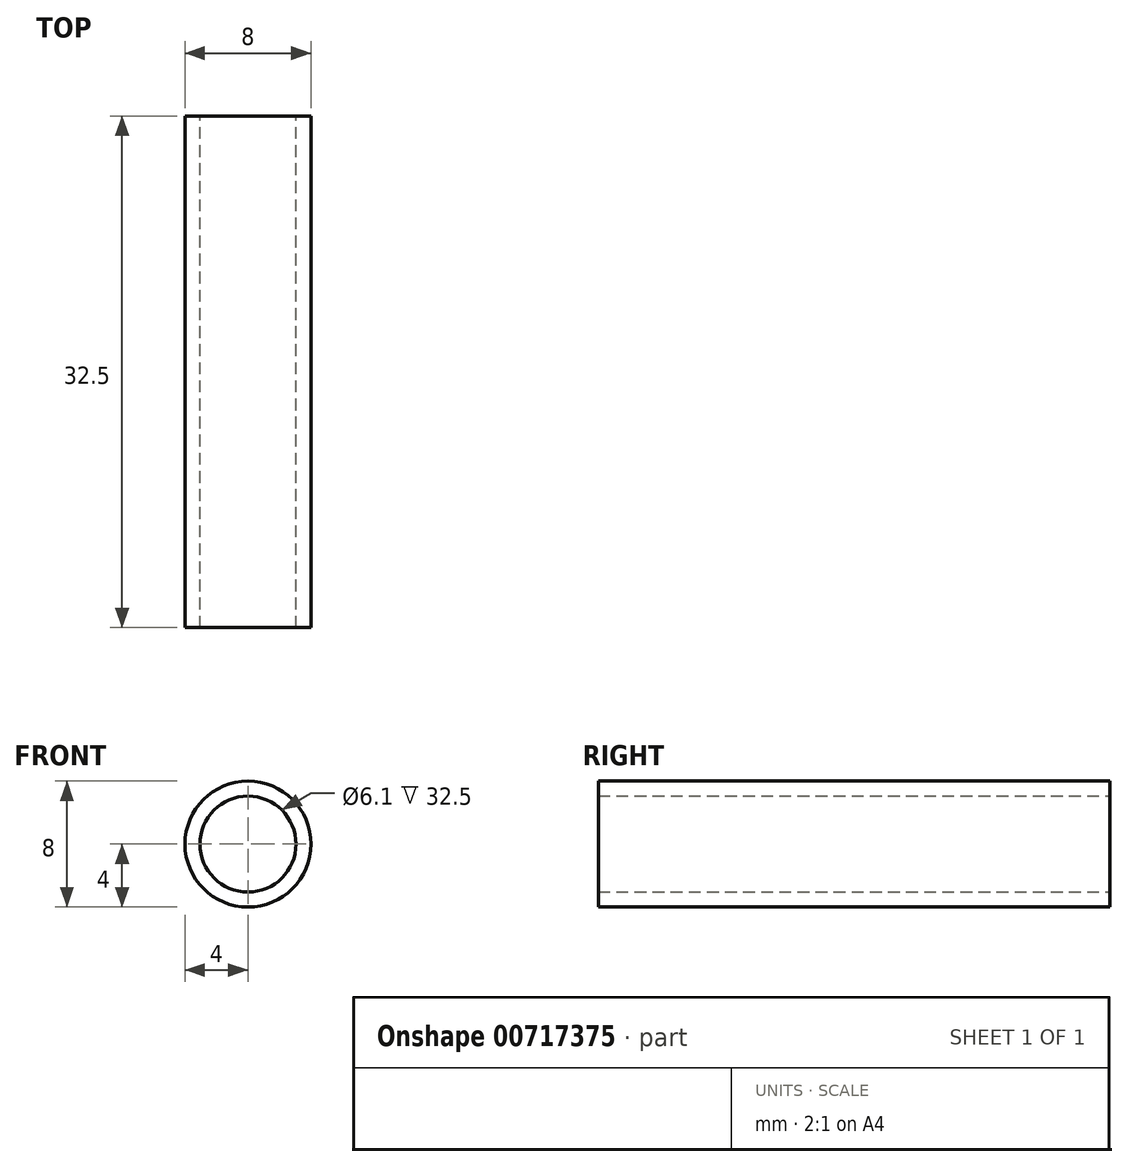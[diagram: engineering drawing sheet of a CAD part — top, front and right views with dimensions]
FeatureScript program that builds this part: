
annotation { "Feature Type Name" : "Feature", "Feature Type Description" : "" }
export const myFeature = defineFeature(function(context is Context, id is Id, definition is map)
    precondition{}
    {
        {
            var Q0;
            Q0=qCreatedBy(makeId("Front.planeOp"),FACE);
            var sketch = newSketch(context, id + "F0", { "sketchPlane" : qUnion([Q0])});
            skCircle(sketch, "E0", {"center": v(0, 0) * mm, "radius": 3.05 * mm});
            skCircle(sketch, "E1", {"center": v(0, 0) * mm, "radius": 4 * mm});
            skSolve(sketch);
        }
        {
            var Q0;
            Q0=makeQuery(id+"F0.imprint","IMPRINT",FACE,{"disambiguationData":[TD([[makeQuery(id+"F0.imprint","IMPRINT",EDGE,{"derivedFrom":sQuery(id+"F0.wireOp",EDGE,"E0")}),-1.0]])]});
            extrude(context, id + "F1", {"entities" : qUnion([Q0]), "depth" : 32.5 * mm, "offsetDistance" : 25 * mm});
        }
    });
